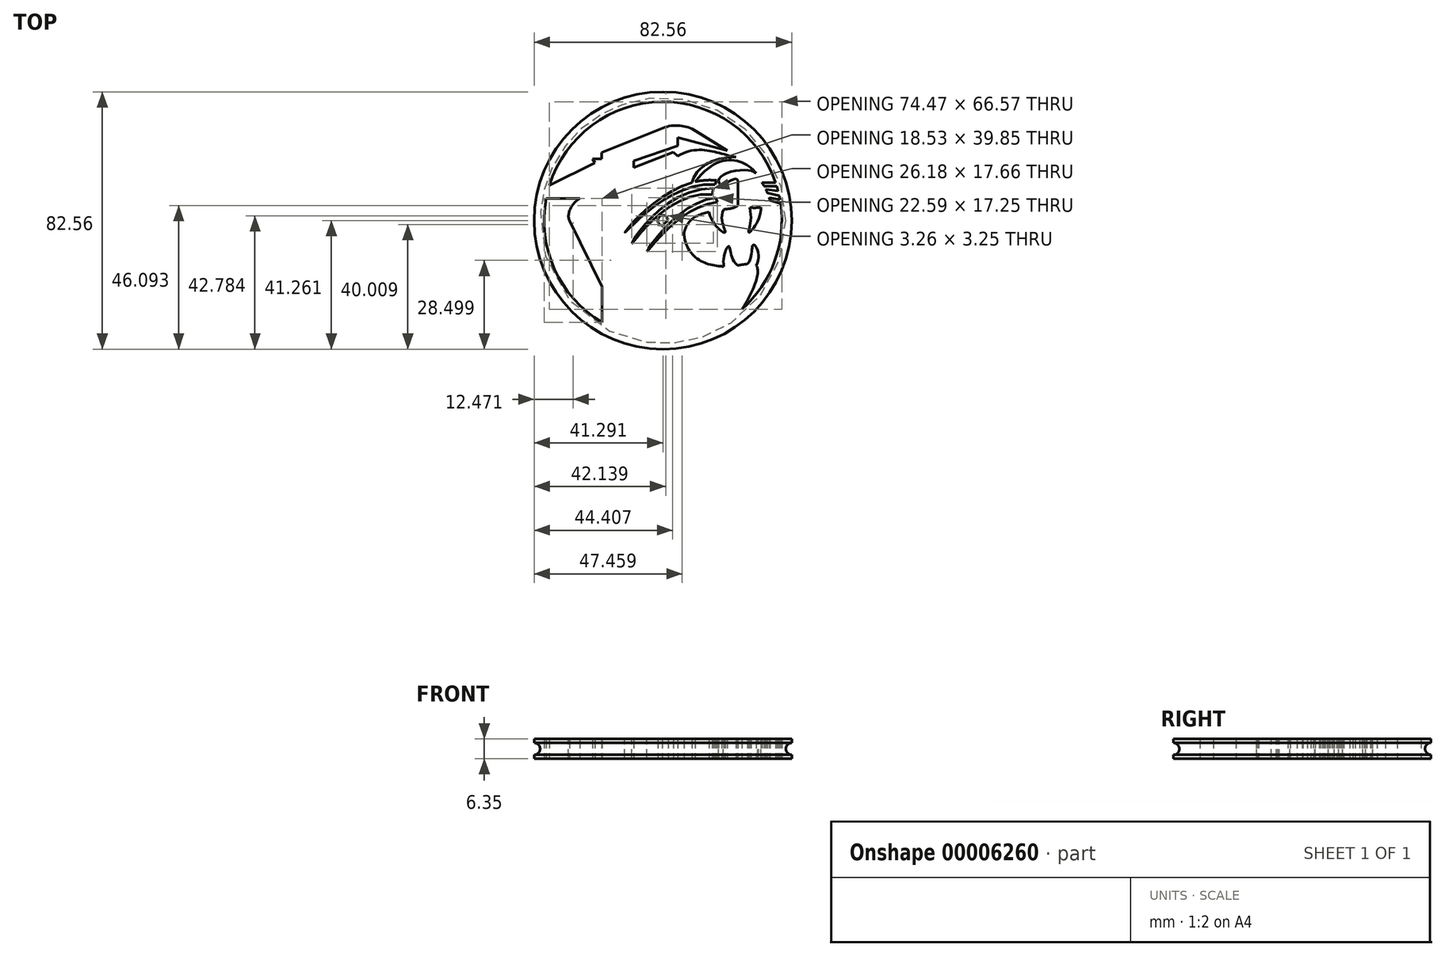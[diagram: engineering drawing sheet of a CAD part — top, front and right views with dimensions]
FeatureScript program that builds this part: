
annotation { "Feature Type Name" : "Feature", "Feature Type Description" : "" }
export const myFeature = defineFeature(function(context is Context, id is Id, definition is map)
    precondition{}
    {
        {
            var Q0;
            Q0=qCreatedBy(makeId("Top.planeOp"),FACE);
            var sketch = newSketch(context, id + "F0", { "sketchPlane" : qUnion([Q0])});
            skCircle(sketch, "E0", {"center": v(0, 0) * mm, "radius": 41.28 * mm});
            skArc(sketch, "E1", {"start": v(1.64, 0.23) * mm, "mid": v(-1.19, 1.15) * mm, "end": v(-0.18, -1.65) * mm});
            skLineSegment(sketch, "E2", {"start": v(-19.54, -32.7) * mm, "end": v(-19.54, -21.25) * mm});
            skLineSegment(sketch, "E3", {"start": v(-19.54, -21.25) * mm, "end": v(-29.91, 0) * mm});
            skLineSegment(sketch, "E4", {"start": v(-26.6, 7.14) * mm, "end": v(-37.42, 7.14) * mm});
            skLineSegment(sketch, "E5", {"start": v(-18.79, -32.25) * mm, "end": v(-5.5, -24.25) * mm});
            skLineSegment(sketch, "E6", {"start": v(-5.5, -24.25) * mm, "end": v(-5.4, -31.69) * mm});
            skLineSegment(sketch, "E7", {"start": v(-5.4, -31.69) * mm, "end": v(8.85, -23.41) * mm});
            skLineSegment(sketch, "E8", {"start": v(8.85, -23.41) * mm, "end": v(8.96, -29.7) * mm});
            skFitSpline(sketch, "E9", {"points": [v(-29.91, 0) * mm, v(-23.1, 7.14) * mm], "startDerivative": vector(-5.28, 8.66) * mm, "endDerivative": vector(10.77, -7.17) * mm});
            skFitSpline(sketch, "E10", {"points": [v(8.96, -29.7) * mm, v(25.32, -28.47) * mm, v(25.32, -28.47) * mm], "startDerivative": vector(47.44, 39.7) * mm, "endDerivative": vector(-1.95, -1.88) * mm});
            skFitSpline(sketch, "E11", {"points": [v(5.73, 0) * mm, v(22.6, -14.56) * mm, v(29.9, -14.48) * mm, v(25.32, -28.47) * mm], "startDerivative": vector(21.9, -103.44) * mm, "endDerivative": vector(-35.34, -54.97) * mm});
            skFitSpline(sketch, "E12", {"points": [v(19.52, -14.73) * mm, v(21.08, -8.23) * mm, v(23.84, -14.4) * mm], "startDerivative": vector(-3.49, 18.5) * mm, "endDerivative": vector(14.85, -13.43) * mm});
            skFitSpline(sketch, "E13", {"points": [v(27.14, -13.91) * mm, v(28.93, -7.84) * mm, v(29.9, -14.48) * mm], "startDerivative": vector(10.02, 12.43) * mm, "endDerivative": vector(-10.7, -20.61) * mm});
            skFitSpline(sketch, "E14", {"points": [v(17.17, 12.86) * mm, v(-12.25, -3.88) * mm, v(16.61, 11.6) * mm], "startDerivative": vector(-89.6, 11.15) * mm, "endDerivative": vector(89, -6.61) * mm});
            skFitSpline(sketch, "E15", {"points": [v(16.9, 7.36) * mm, v(-5.11, -9.9) * mm, v(17.47, 5.88) * mm], "startDerivative": vector(-73.1, -8.45) * mm, "endDerivative": vector(72.62, 6.22) * mm});
            skFitSpline(sketch, "E16", {"points": [v(16.21, 10.34) * mm, v(-9.95, -7.33) * mm, v(15.8, 8.37) * mm], "startDerivative": vector(-96.18, 0.86) * mm, "endDerivative": vector(86.53, -8.08) * mm});
            skLineSegment(sketch, "E17", {"start": v(17.17, 12.86) * mm, "end": v(16.61, 11.6) * mm});
            skLineSegment(sketch, "E18", {"start": v(15.8, 8.37) * mm, "end": v(16.21, 10.34) * mm});
            skLineSegment(sketch, "E19", {"start": v(25.17, -28.06) * mm, "end": v(25.17, -28.6) * mm});
            skArc(sketch, "E20.trimOffspring", {"start": v(25.32, -28.47) * mm, "mid": v(25.32, -28.47) * mm, "end": v(25.32, -28.47) * mm});
            skFitSpline(sketch, "E21", {"points": [v(19.52, -14.73) * mm, v(6.73, -4.5) * mm], "startDerivative": vector(-16.71, 0.55) * mm, "endDerivative": vector(-2.84, 23.57) * mm});
            skFitSpline(sketch, "E22", {"points": [v(6.73, -4.5) * mm, v(24.02, 5.49) * mm], "startDerivative": vector(3.4, 31.15) * mm, "endDerivative": vector(-2.16, 10.6) * mm});
            skLineSegment(sketch, "E23", {"start": v(16.9, 7.36) * mm, "end": v(17.47, 5.88) * mm});
            skFitSpline(sketch, "E24", {"points": [v(14.73, 2.8) * mm, v(19.94, -3.75) * mm, v(19.45, 3.55) * mm], "startDerivative": vector(6.41, -26.93) * mm, "endDerivative": vector(10.42, 21.37) * mm});
            skFitSpline(sketch, "E25", {"points": [v(27.67, 4.58) * mm, v(27.6, -3.8) * mm, v(31.36, 4.4) * mm], "startDerivative": vector(8.56, -28.07) * mm, "endDerivative": vector(-2.05, 22.89) * mm});
            skLineSegment(sketch, "E26", {"start": v(24.02, 5.49) * mm, "end": v(24.02, 11.88) * mm});
            skLineSegment(sketch, "E27", {"start": v(25.3, 4.42) * mm, "end": v(25.3, 11.7) * mm});
            skFitSpline(sketch, "E28", {"points": [v(25.3, 4.42) * mm, v(34.47, 6.01) * mm, v(31.22, 13.97) * mm], "startDerivative": vector(35.54, -5.04) * mm, "endDerivative": vector(-23.07, 27.5) * mm});
            skFitSpline(sketch, "E29", {"points": [v(24.02, 11.88) * mm, v(23.68, 13.31) * mm, v(21.16, 12.54) * mm, v(18.79, 11.5) * mm, v(17.83, 12.73) * mm, v(20.32, 15.16) * mm, v(27.31, 16.14) * mm, v(30.32, 14.85) * mm, v(31.22, 13.3) * mm, v(28.65, 13.48) * mm, v(27.36, 13.61) * mm, v(26.07, 13.6) * mm, v(25.3, 11.7) * mm], "startDerivative": vector(0.46, 29.16) * mm, "endDerivative": vector(-6.46, -31.38) * mm});
            skFitSpline(sketch, "E30", {"points": [v(31.35, 3.56) * mm, v(34.49, 4.23) * mm, v(30.92, 13.18) * mm, v(30.8, 13.18) * mm], "startDerivative": vector(9.9, -8.27) * mm, "endDerivative": vector(0.2, -0.12) * mm});
            skLineSegment(sketch, "E31", {"start": v(31.74, 12.2) * mm, "end": v(36.1, 12.2) * mm});
            skLineSegment(sketch, "E32", {"start": v(32.43, 11.03) * mm, "end": v(36.47, 11.03) * mm});
            skLineSegment(sketch, "E33", {"start": v(32.94, 10.04) * mm, "end": v(36.9, 9.48) * mm});
            skLineSegment(sketch, "E34", {"start": v(36.9, 9.48) * mm, "end": v(36.7, 9.72) * mm});
            skLineSegment(sketch, "E35", {"start": v(33.49, 8.85) * mm, "end": v(37.25, 8.02) * mm});
            skLineSegment(sketch, "E36", {"start": v(34.05, 7.37) * mm, "end": v(37.5, 6.69) * mm});
            skLineSegment(sketch, "E37", {"start": v(34.32, 6.45) * mm, "end": v(37.71, 5.42) * mm});
            skCircle(sketch, "E38", {"center": v(0, 0) * mm, "radius": 38.1 * mm});
            skFitSpline(sketch, "E39", {"points": [v(23.92, 20.34) * mm, v(9.34, 12.18) * mm], "startDerivative": vector(-17.59, 0.84) * mm, "endDerivative": vector(-4.58, -18.21) * mm});
            skFitSpline(sketch, "E40", {"points": [v(10.31, 12.43) * mm, v(29.92, 15.19) * mm], "startDerivative": vector(23.24, 30.99) * mm, "endDerivative": vector(11.7, -13.67) * mm});
            skLineSegment(sketch, "E41", {"start": v(23.92, 20.34) * mm, "end": v(10.6, 28.71) * mm});
            skLineSegment(sketch, "E42", {"start": v(20.6, 22.43) * mm, "end": v(4.78, 26.62) * mm});
            skLineSegment(sketch, "E43", {"start": v(4.78, 26.62) * mm, "end": v(4.78, 23.96) * mm});
            skLineSegment(sketch, "E44", {"start": v(4.78, 23.96) * mm, "end": v(-9.3, 19.16) * mm});
            skLineSegment(sketch, "E45", {"start": v(-9.3, 19.16) * mm, "end": v(-9.3, 16.97) * mm});
            skLineSegment(sketch, "E46", {"start": v(-9.3, 16.97) * mm, "end": v(3.35, 21.92) * mm});
            skLineSegment(sketch, "E47", {"start": v(3.35, 21.92) * mm, "end": v(4.69, 20.69) * mm});
            skFitSpline(sketch, "E48", {"points": [v(4.69, 20.69) * mm, v(23.38, 20.36) * mm], "startDerivative": vector(20.58, 12.42) * mm, "endDerivative": vector(16.84, -3) * mm});
            skLineSegment(sketch, "E49", {"start": v(-36.37, 11.34) * mm, "end": v(-21.83, 18.45) * mm});
            skLineSegment(sketch, "E50", {"start": v(-21.83, 18.45) * mm, "end": v(-22.5, 19.84) * mm});
            skLineSegment(sketch, "E51", {"start": v(-22.5, 19.84) * mm, "end": v(-19.66, 19.84) * mm});
            skLineSegment(sketch, "E52", {"start": v(-19.66, 19.84) * mm, "end": v(-19.66, 21.85) * mm});
            skLineSegment(sketch, "E53", {"start": v(-19.66, 21.85) * mm, "end": v(0, 29.68) * mm});
            skPoint(sketch, "E54.visualSharp", {"position": v(5.54, 31.88) * mm});
            skArc(sketch, "E54.filletArc", {"start": v(10.6, 28.71) * mm, "mid": v(5.41, 30.46) * mm, "end": v(0, 29.68) * mm});
            skLineSegment(sketch, "E55", {"start": v(-18.79, -32.25) * mm, "end": v(-19.15, -32.93) * mm});
            skLineSegment(sketch, "E56", {"start": v(25.53, -28.14) * mm, "end": v(25.64, -28.18) * mm});
            skLineSegment(sketch, "E57", {"start": v(-0.18, -1.65) * mm, "end": v(1.64, 0.23) * mm});
            skSolve(sketch);
        }
        {
            var Q0;
            Q0=qSketchRegion(id+"F0",true);
            var Q1;
            {var subQ0=sQuery(id+"F0.wireOp",EDGE,"E12");Q1=makeQuery(id+"F0.imprint","IMPRINT",FACE,{"disambiguationData":[TD([[makeQuery(id+"F0.imprint","IMPRINT",EDGE,{"derivedFrom":subQ0}),-1.0]])]});}
            var Q2;
            {var subQ0=sQuery(id+"F0.wireOp",EDGE,"E13");Q2=makeQuery(id+"F0.imprint","IMPRINT",FACE,{"disambiguationData":[TD([[makeQuery(id+"F0.imprint","IMPRINT",EDGE,{"derivedFrom":subQ0}),-1.0]])]});}
            var Q3;
            {var subQ0=sQuery(id+"F0.wireOp",EDGE,"9d78af66-d1aa-41fc-a9f2-600b2c9dbe75");Q3=makeQuery(id+"F0.imprint","IMPRINT",FACE,{"disambiguationData":[TD([[makeQuery(id+"F0.imprint","IMPRINT",EDGE,{"derivedFrom":subQ0}),1.0]])]});}
            var Q4;
            {var subQ1=sQuery(id+"F0.wireOp",EDGE,"91f76ec8-b100-4449-a675-d3caf3ae3a79");Q4=makeQuery(id+"F0.imprint","IMPRINT",FACE,{"disambiguationData":[TD([[makeQuery(id+"F0.imprint","IMPRINT",EDGE,{"derivedFrom":subQ1}),1.0]])]});}
            var Q5;
            {var subQ0=sQuery(id+"F0.wireOp",EDGE,"c7dc1507-02c0-4cf5-9992-08b9f5c6a8ae");Q5=makeQuery(id+"F0.imprint","IMPRINT",FACE,{"disambiguationData":[TD([[makeQuery(id+"F0.imprint","IMPRINT",EDGE,{"derivedFrom":subQ0}),-1.0]])]});}
            var Q6;
            {var subQ0=sQuery(id+"F0.wireOp",EDGE,"E24");Q6=makeQuery(id+"F0.imprint","IMPRINT",FACE,{"disambiguationData":[TD([[makeQuery(id+"F0.imprint","IMPRINT",EDGE,{"derivedFrom":subQ0}),1.0]])]});}
            var Q7;
            {var subQ8=sQuery(id+"F0.wireOp",EDGE,"E25");Q7=makeQuery(id+"F0.imprint","IMPRINT",FACE,{"disambiguationData":[TD([[makeQuery(id+"F0.imprint","IMPRINT",EDGE,{"derivedFrom":subQ8}),1.0]])]});}
            var Q8;
            {var subQ0=sQuery(id+"F0.wireOp",EDGE,"E36");Q8=makeQuery(id+"F0.imprint","IMPRINT",FACE,{"disambiguationData":[TD([[makeQuery(id+"F0.imprint","IMPRINT",EDGE,{"derivedFrom":subQ0}),-1.0]])]});}
            var Q9;
            {var subQ1=sQuery(id+"F0.wireOp",EDGE,"E33");Q9=makeQuery(id+"F0.imprint","IMPRINT",FACE,{"disambiguationData":[TD([[makeQuery(id+"F0.imprint","IMPRINT",EDGE,{"derivedFrom":subQ1}),-1.0]])]});}
            var Q10;
            {var subQ1=sQuery(id+"F0.wireOp",EDGE,"E31");Q10=makeQuery(id+"F0.imprint","IMPRINT",FACE,{"disambiguationData":[TD([[makeQuery(id+"F0.imprint","IMPRINT",EDGE,{"derivedFrom":subQ1}),-1.0]])]});}
            var Q11;
            {var subQ21=sQuery(id+"F0.wireOp",EDGE,"E2");Q11=makeQuery(id+"F0.imprint","IMPRINT",FACE,{"disambiguationData":[TD([[makeQuery(id+"F0.imprint","IMPRINT",EDGE,{"derivedFrom":subQ21}),-1.0]])]});}
            var Q12;
            {var subQ0=sQuery(id+"F0.wireOp",EDGE,"E57");Q12=makeQuery(id+"F0.imprint","IMPRINT",FACE,{"disambiguationData":[TD([[makeQuery(id+"F0.imprint","IMPRINT",EDGE,{"derivedFrom":subQ0}),-1.0]])]});}
            extrude(context, id + "F1", {"entities" : qUnion([Q0, Q1, Q2, Q3, Q4, Q5, Q6, Q7, Q8, Q9, Q10, Q11, Q12]), "depth" : 6.35 * mm});
        }
        {
            var Q0;
            Q0=qCreatedBy(makeId("Right.planeOp"),FACE);
            var sketch = newSketch(context, id + "F2", { "sketchPlane" : qUnion([Q0])});
            skLineSegment(sketch, "E58", {"start": v(0, 0) * mm, "end": v(0, 8.3) * mm});
            skCircle(sketch, "E59", {"center": v(41.28, 3.18) * mm, "radius": 1.9 * mm});
            skSolve(sketch);
        }
        {
            var Q0;
            Q0=makeQuery(id+"F2.imprint","IMPRINT",FACE,{"disambiguationData":[TD([[makeQuery(id+"F2.imprint","IMPRINT",EDGE,{"derivedFrom":sQuery(id+"F2.wireOp",EDGE,"E59")}),1.0]])]});
            var Q1;
            Q1=sQuery(id+"F2.wireOp",EDGE,"E58");
            revolve(context, id + "F3", {"operationType" : NewBodyOperationType.REMOVE, "entities" : qUnion([Q0]), "axis" : qUnion([Q1]), "revolveType" : RevolveType.FULL, "oppositeDirection" : true});
        }
    });
